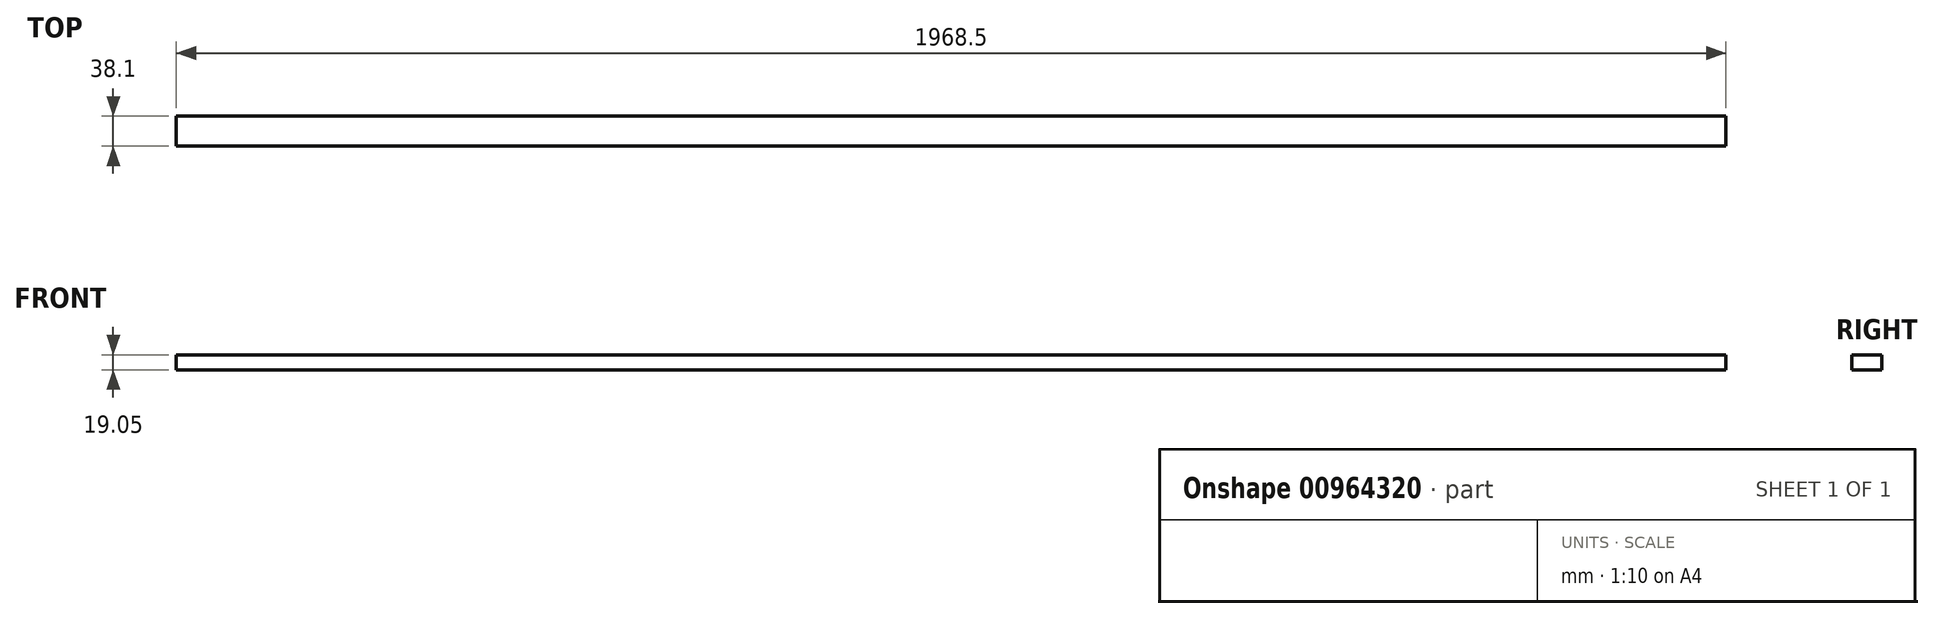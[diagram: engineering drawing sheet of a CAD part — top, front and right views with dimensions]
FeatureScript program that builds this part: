
annotation { "Feature Type Name" : "Feature", "Feature Type Description" : "" }
export const myFeature = defineFeature(function(context is Context, id is Id, definition is map)
    precondition{}
    {
        {
            var Q0;
            Q0=qCreatedBy(makeId("Right.planeOp"),FACE);
            var sketch = newSketch(context, id + "F0", { "sketchPlane" : qUnion([Q0])});
            skLineSegment(sketch, "E0.bottom", {"start": v(0, 0) * mm, "end": v(-38.1, 0) * mm});
            skLineSegment(sketch, "E0.top", {"start": v(0, 19.05) * mm, "end": v(-38.1, 19.05) * mm});
            skLineSegment(sketch, "E0.left", {"start": v(0, 0) * mm, "end": v(0, 19.05) * mm});
            skLineSegment(sketch, "E0.right", {"start": v(-38.1, 0) * mm, "end": v(-38.1, 19.05) * mm});
            skSolve(sketch);
        }
        {
            var Q0;
            Q0 = qSketchRegion(id + "F0", true);
            extrude(context, id + "F1", {"entities" : qUnion([Q0]), "endBound" : BoundingType.SYMMETRIC, "depth" : 1968.5 * mm, "offsetDistance" : 25.4 * mm});
        }
    });
